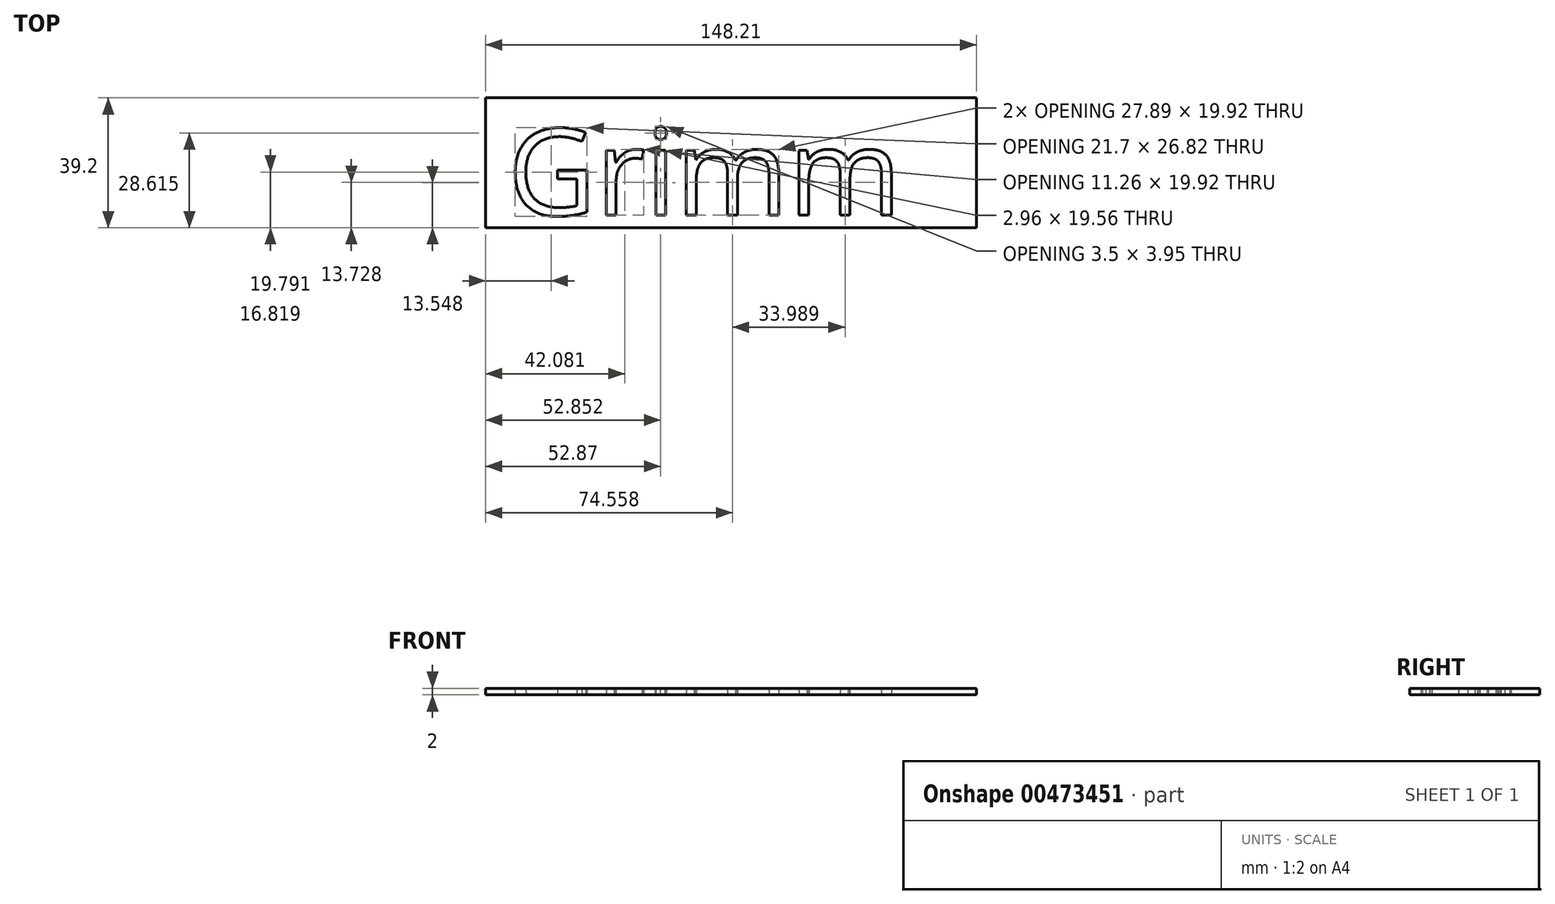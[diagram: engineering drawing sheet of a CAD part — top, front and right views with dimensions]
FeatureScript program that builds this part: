
annotation { "Feature Type Name" : "Feature", "Feature Type Description" : "" }
export const myFeature = defineFeature(function(context is Context, id is Id, definition is map)
    precondition{}
    {
        {
            var Q0;
            Q0=qCreatedBy(makeId("Top.planeOp"),FACE);
            var sketch = newSketch(context, id + "F0", { "sketchPlane" : qUnion([Q0])});
            skLineSegment(sketch, "E0.bottom", {"start": v(-73.03, 24.43) * mm, "end": v(75.18, 24.43) * mm});
            skLineSegment(sketch, "E0.top", {"start": v(-73.03, -14.77) * mm, "end": v(75.18, -14.77) * mm});
            skLineSegment(sketch, "E0.left", {"start": v(-73.03, 24.43) * mm, "end": v(-73.03, -14.77) * mm});
            skLineSegment(sketch, "E0.right", {"start": v(75.18, 24.43) * mm, "end": v(75.18, -14.77) * mm});
            skText(sketch, "E1", { "text": "Grimm", "fontName": "OpenSans-Regular.ttf"});
            const initialGuessF0  = {"E1": [-0.06632, -0.011, 1, 0, 0.02631]};
            skSetInitialGuess(sketch, initialGuessF0);
            skSolve(sketch);
        }
        {
            var Q0;
            Q0=makeQuery(id+"F0.imprint","IMPRINT",FACE,{"disambiguationData":[TD([[makeQuery(id+"F0.imprint","IMPRINT",EDGE,{"derivedFrom":sQuery(id+"F0.wireOp",EDGE,"E0.bottom")}),-1.0]])]});
            extrude(context, id + "F1", {"entities" : qUnion([Q0]), "depth" : 2 * mm});
        }
    });
